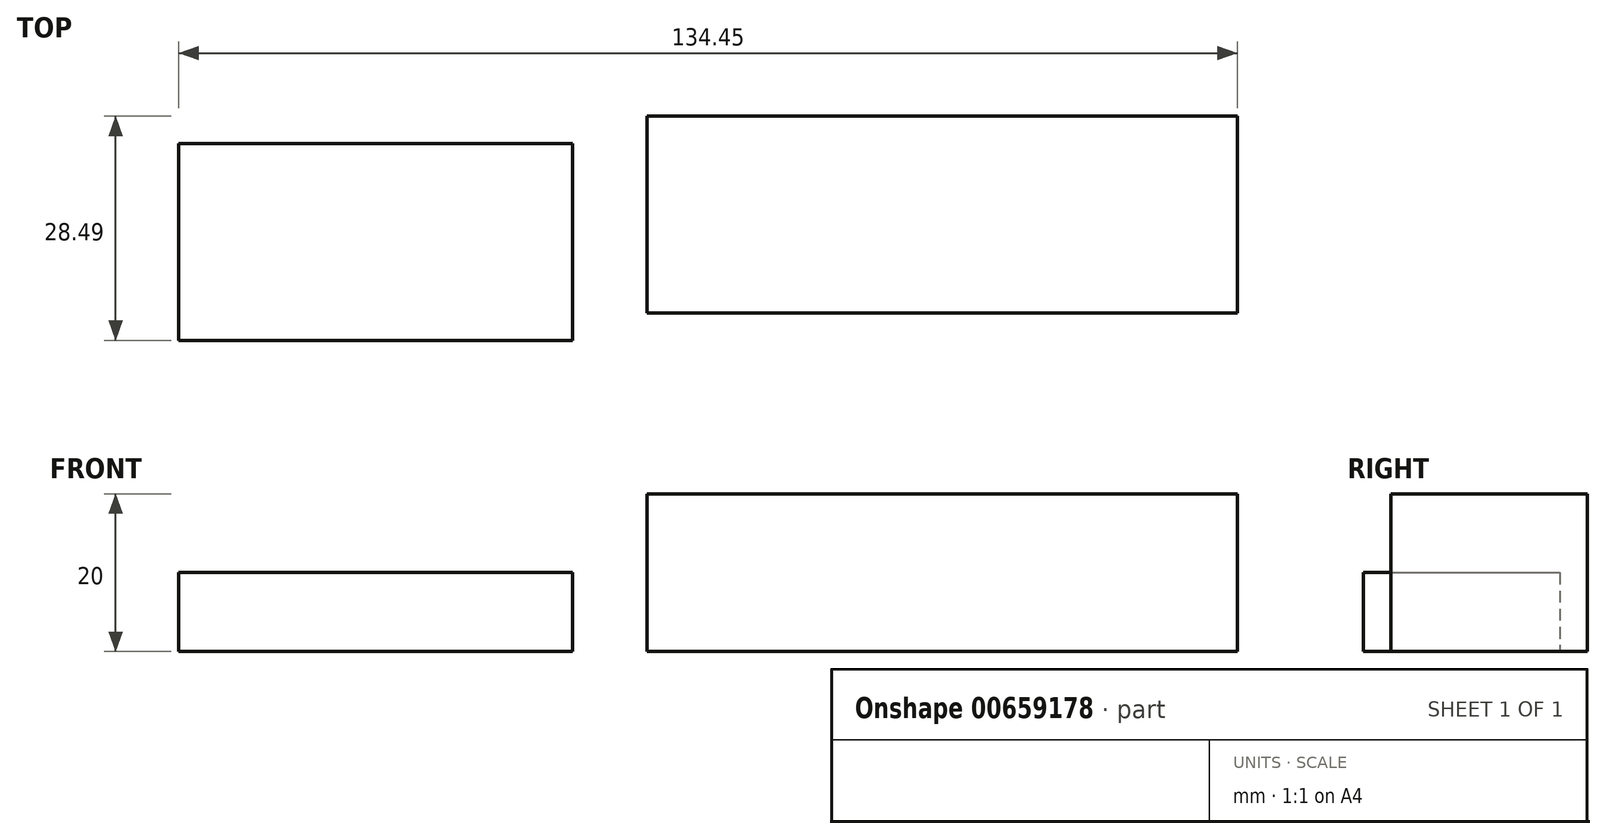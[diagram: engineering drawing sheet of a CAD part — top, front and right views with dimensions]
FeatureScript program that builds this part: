
annotation { "Feature Type Name" : "Feature", "Feature Type Description" : "" }
export const myFeature = defineFeature(function(context is Context, id is Id, definition is map)
    precondition{}
    {
        {
            assignVariable(context, id + "F0", {"name" : "thickness", "anyValue" : 10});
        }
        {
            var Q0;
            Q0=qCreatedBy(makeId("Top.planeOp"),FACE);
            var sketch = newSketch(context, id + "F1", { "sketchPlane" : qUnion([Q0])});
            skLineSegment(sketch, "E0.bottom", {"start": v(0, 0) * mm, "end": v(-50, 0) * mm});
            skLineSegment(sketch, "E0.top", {"start": v(0, 25) * mm, "end": v(-50, 25) * mm});
            skLineSegment(sketch, "E0.left", {"start": v(0, 0) * mm, "end": v(0, 25) * mm});
            skLineSegment(sketch, "E0.right", {"start": v(-50, 0) * mm, "end": v(-50, 25) * mm});
            skSolve(sketch);
        }
        {
            var Q0;
            Q0 = qSketchRegion(id + "F1", true);
            extrude(context, id + "F2", {"entities" : qUnion([Q0]), "depth" : (getVariable(context, 'thickness')) * mm, "offsetDistance" : 25 * mm});
        }
        {
            var Q0;
            Q0=qCreatedBy(makeId("Top.planeOp"),FACE);
            var sketch = newSketch(context, id + "F3", { "sketchPlane" : qUnion([Q0])});
            skLineSegment(sketch, "E1.bottom", {"start": v(84.45, 3.5) * mm, "end": v(9.45, 3.5) * mm});
            skLineSegment(sketch, "E1.top", {"start": v(84.45, 28.5) * mm, "end": v(9.45, 28.5) * mm});
            skLineSegment(sketch, "E1.left", {"start": v(84.45, 3.5) * mm, "end": v(84.45, 28.5) * mm});
            skLineSegment(sketch, "E1.right", {"start": v(9.45, 3.5) * mm, "end": v(9.45, 28.5) * mm});
            skSolve(sketch);
        }
        {
            var Q0;
            Q0=makeQuery(id+"F3.imprint","IMPRINT",FACE,{"disambiguationData":[TD([[makeQuery(id+"F3.imprint","IMPRINT",EDGE,{"derivedFrom":sQuery(id+"F3.wireOp",EDGE,"E1.bottom")}),-1.0]])]});
            extrude(context, id + "F4", {"entities" : qUnion([Q0]), "depth" : getVariable(context, 'thickness') * 2 * mm, "offsetDistance" : 25 * mm});
        }
    });
